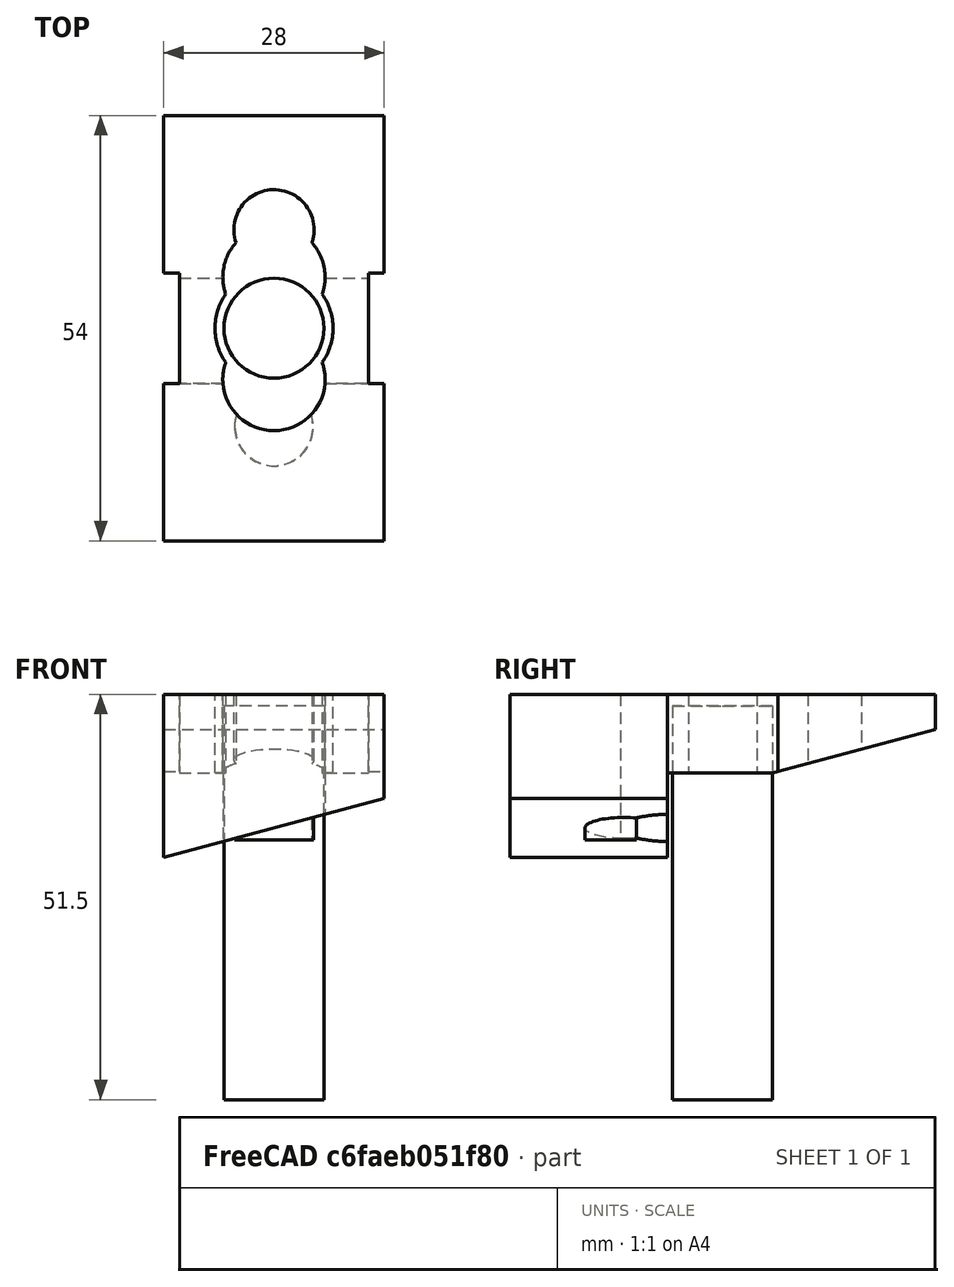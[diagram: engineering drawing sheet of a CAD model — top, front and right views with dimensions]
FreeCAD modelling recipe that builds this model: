
FCSTD DOCUMENT  (FreeCAD 0.20R29410 (Git))
Label: laddleFour3
License: All rights reserved
LicenseURL: http://en.wikipedia.org/wiki/All_rights_reserved
objects: Part::Cylinder×11, Part::MultiFuse×10, Part::Box×7, Part::Cut×6, Part::Feature×1
note: 35 computed .brp shape members not serialized (recipe doc carries the construction recipe); baked Part::Feature solids carry a one-line shape summary decoded from their .brp

FEATURE [Part::Box] Box  label="Cube"
  AttacherType = Attacher::AttachEngine3D
  Height = 30
  Length = 40
  Placement = pos=(-19.5582,7,39.7598) rot=(0,1,0;0.261799rad)
  Width = 20
FEATURE [Part::Box] Box001  label="Cube001"
  AttacherType = Attacher::AttachEngine3D
  Height = 30
  Length = 40
  Placement = pos=(-19.5582,7,39.7598) rot=(0,1,0;0.261799rad)
  Width = 20
FEATURE [Part::Cylinder] Cylinder001
  Angle = 360
  AttacherType = Attacher::AttachEngine3D
  FirstAngle = 0
  Height = 50
  Placement = pos=(0,12.5,0) rot=(0,0,1;0rad)
  Radius = 5
  SecondAngle = 0
FEATURE [Part::Cylinder] Cylinder003  label="bevilPin"
  Angle = 360
  AttacherType = Attacher::AttachEngine3D
  FirstAngle = 0
  Height = 50
  Radius = 6.35
  SecondAngle = 0
FEATURE [Part::Cylinder] Cylinder004  label="bevilPin001"
  Angle = 360
  AttacherType = Attacher::AttachEngine3D
  FirstAngle = 0
  Height = 50
  Radius = 6.35
  SecondAngle = 0
FEATURE [Part::Cylinder] Cylinder005
  Angle = 360
  AttacherType = Attacher::AttachEngine3D
  FirstAngle = 0
  Height = 50
  Placement = pos=(0,12.5,0) rot=(0,0,1;0rad)
  Radius = 5
  SecondAngle = 0
FEATURE [Part::Cylinder] Cylinder006  label="bevilPin002"
  Angle = 360
  AttacherType = Attacher::AttachEngine3D
  FirstAngle = 0
  Height = 50
  Radius = 6.35
  SecondAngle = 0
FEATURE [Part::MultiFuse] Fusion
  Shapes = -> [Cylinder001,Box]
FEATURE [Part::MultiFuse] Fusion001
  Shapes = -> [Fusion,Cylinder004]
FEATURE [Part::MultiFuse] Fusion002
  Shapes = -> [Cylinder005,Box001]
FEATURE [Part::MultiFuse] Fusion003
  Placement = pos=(0,0,0) rot=(0,0,1;3.14159rad)
  Shapes = -> [Fusion002,Cylinder006]
FEATURE [Part::MultiFuse] Fusion004
  Shapes = -> [Fusion003,Fusion001]
FEATURE [Part::Box] Box002  label="Cube002"
  AttacherType = Attacher::AttachEngine3D
  Height = 10
  Length = 24
  Placement = pos=(-12,-13,41.5) rot=(0,0,1;0rad)
  Width = 39
FEATURE [Part::Box] Box003  label="Cube003"
  AttacherType = Attacher::AttachEngine3D
  Height = 20
  Length = 57
  Placement = pos=(-29.5,-29,51.5) rot=(0,0,1;0rad)
  Width = 59
FEATURE [Part::MultiFuse] Fusion005
  Shapes = -> [Box002,Fusion004]
FEATURE [Part::Cut] Cut
  Base = -> Fusion005
  Tool = -> Box003
FEATURE [Part::Cylinder] Cylinder007  label="bevilPin003"
  Angle = 360
  AttacherType = Attacher::AttachEngine3D
  FirstAngle = 0
  Height = 70
  Radius = 7.5
  SecondAngle = 0
FEATURE [Part::Cylinder] Cylinder008
  Angle = 360
  AttacherType = Attacher::AttachEngine3D
  FirstAngle = 0
  Height = 70
  Placement = pos=(0,12.5,0) rot=(0,0,1;0rad)
  Radius = 5.1
  SecondAngle = 0
FEATURE [Part::Cylinder] Cylinder009
  Angle = 360
  AttacherType = Attacher::AttachEngine3D
  FirstAngle = 0
  Height = 70
  Placement = pos=(0,6.5,0) rot=(0,0,1;0rad)
  Radius = 6.5
  SecondAngle = 0
FEATURE [Part::MultiFuse] Fusion006
  Shapes = -> [Cylinder009,Cylinder007]
FEATURE [Part::Cylinder] Cylinder010  label="bevilPin004"
  Angle = 360
  AttacherType = Attacher::AttachEngine3D
  FirstAngle = 0
  Height = 70
  Radius = 7.5
  SecondAngle = 0
FEATURE [Part::Cylinder] Cylinder011
  Angle = 360
  AttacherType = Attacher::AttachEngine3D
  FirstAngle = 0
  Height = 70
  Placement = pos=(0,6.5,0) rot=(0,0,1;0rad)
  Radius = 6.5
  SecondAngle = 0
FEATURE [Part::MultiFuse] Fusion007
  Placement = pos=(0,0,0) rot=(0,0,1;3.14159rad)
  Shapes = -> [Cylinder011,Cylinder010]
FEATURE [Part::MultiFuse] Fusion008
  Shapes = -> [Fusion007,Fusion006]
FEATURE [Part::Cut] Cut001
  Base = -> Cut
  Tool = -> Cylinder008
FEATURE [Part::Cut] Cut002
  Base = -> Cut001
  Tool = -> Fusion008
FEATURE [Part::Cylinder] Cylinder012  label="bevilPin005"
  Angle = 360
  AttacherType = Attacher::AttachEngine3D
  FirstAngle = 0
  Height = 50
  Placement = pos=(0,-12.5,-17) rot=(0,0,1;0rad)
  Radius = 5.1
  SecondAngle = 0
FEATURE [Part::Cut] Cut003
  Base = -> Cut002
  Tool = -> Cylinder012
FEATURE [Part::Box] Box004  label="Cube004"
  AttacherType = Attacher::AttachEngine3D
  Height = 19
  Length = 50
  Placement = pos=(-24,7.96593,22.2588) rot=(1,0,0;0.261799rad)
  Width = 30
FEATURE [Part::Cut] Cut004
  Base = -> Cut003
  Tool = -> Box004
FEATURE [Part::Box] Box005  label="Cube005"
  AttacherType = Attacher::AttachEngine3D
  Height = 30
  Length = 12
  Placement = pos=(14,-29,23) rot=(0,0,1;0rad)
  Width = 60
FEATURE [Part::Box] Box006  label="Cube006"
  AttacherType = Attacher::AttachEngine3D
  Height = 30
  Length = 12
  Placement = pos=(-26,-29,23) rot=(0,0,1;0rad)
  Width = 60
FEATURE [Part::MultiFuse] Fusion009
  Shapes = -> [Box006,Box005]
FEATURE [Part::Cut] Cut005
  Base = -> Cut004
  Tool = -> Fusion009
FEATURE [Part::Feature] Cut005_solid  label="Cut005 (Solid)"
  shape: bbox 28 x 54 x 20.73 mm, 34 faces (baked)
